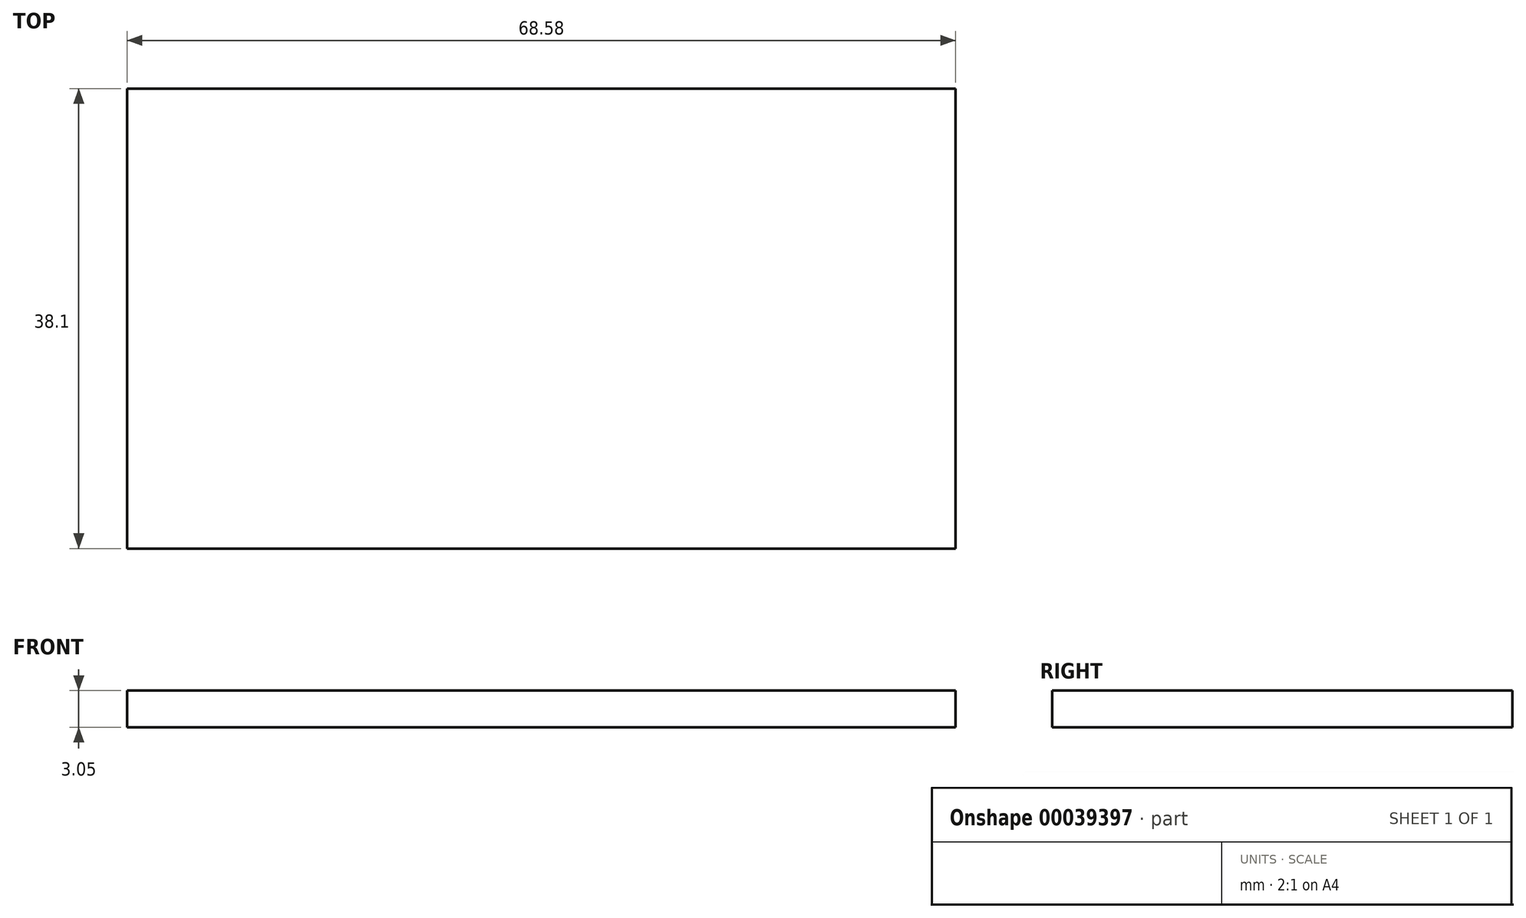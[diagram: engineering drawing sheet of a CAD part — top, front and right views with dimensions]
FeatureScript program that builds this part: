
annotation { "Feature Type Name" : "Feature", "Feature Type Description" : "" }
export const myFeature = defineFeature(function(context is Context, id is Id, definition is map)
    precondition{}
    {
        {
            var Q0;
            Q0=qCreatedBy(makeId("Top.planeOp"),FACE);
            var sketch = newSketch(context, id + "F0", { "sketchPlane" : qUnion([Q0])});
            skLineSegment(sketch, "E0.bottom", {"start": v(0, 0) * mm, "end": v(68.58, 0) * mm});
            skLineSegment(sketch, "E0.top", {"start": v(0, 38.1) * mm, "end": v(68.58, 38.1) * mm});
            skLineSegment(sketch, "E0.left", {"start": v(0, 0) * mm, "end": v(0, 38.1) * mm});
            skLineSegment(sketch, "E0.right", {"start": v(68.58, 0) * mm, "end": v(68.58, 38.1) * mm});
            skSolve(sketch);
        }
        {
            var Q0;
            Q0 = qSketchRegion(id + "F0", true);
            extrude(context, id + "F1", {"entities" : qUnion([Q0]), "depth" : 3.05 * mm});
        }
    });
